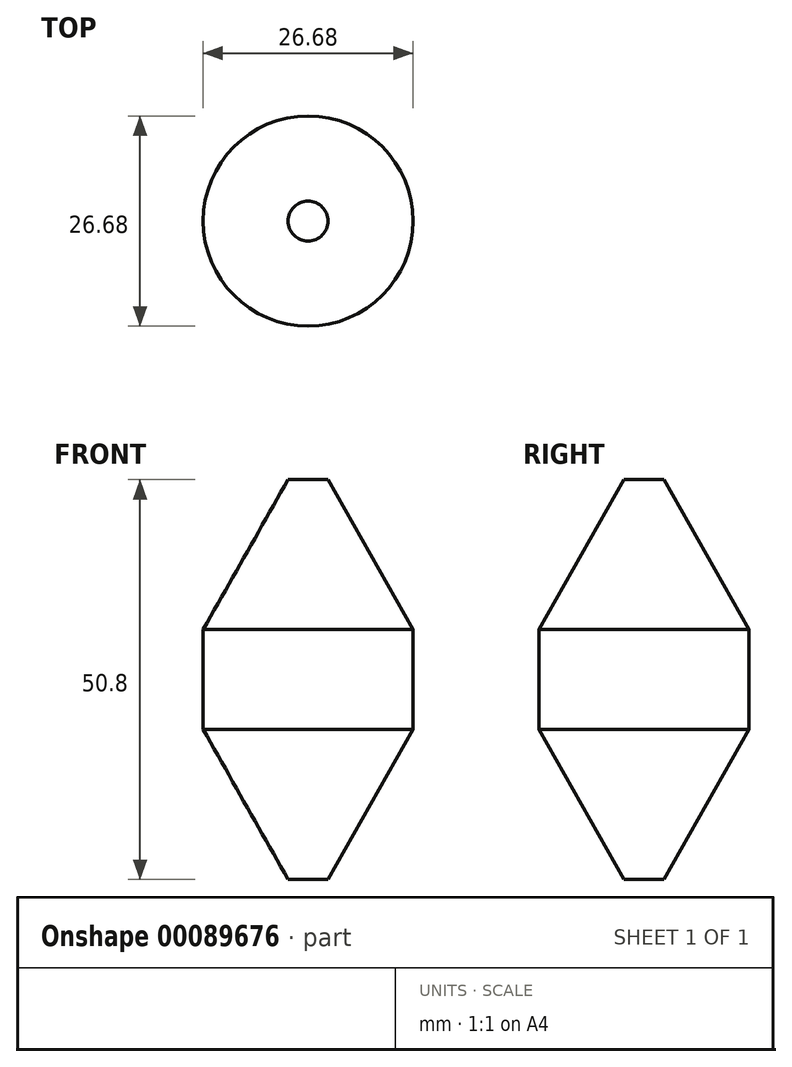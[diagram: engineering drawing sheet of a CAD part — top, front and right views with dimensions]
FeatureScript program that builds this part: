
annotation { "Feature Type Name" : "Feature", "Feature Type Description" : "" }
export const myFeature = defineFeature(function(context is Context, id is Id, definition is map)
    precondition{}
    {
        {
            var Q0;
            Q0=qCreatedBy(makeId("Top.planeOp"),FACE);
            var sketch = newSketch(context, id + "F0", { "sketchPlane" : qUnion([Q0])});
            skCircle(sketch, "E0", {"center": v(0, 0) * mm, "radius": 13.34 * mm});
            skSolve(sketch);
        }
        {
            var Q0;
            Q0 = qSketchRegion(id + "F0", true);
            extrude(context, id + "F1", {"entities" : qUnion([Q0]), "depth" : 6.35 * mm});
        }
        {
            var Q0;
            Q0=qCreatedBy(makeId("Right.planeOp"),FACE);
            cPlane(context, id + "F2", {"entities" : qUnion([Q0]), "cplaneType" : CPlaneType.OFFSET, "offset" : 8.9 * mm, "width" : 152.4 * mm, "height" : 152.4 * mm});
        }
        {
            var Q0;
            Q0=qCreatedBy(makeId("Right.planeOp"),FACE);
            var sketch = newSketch(context, id + "F4", { "sketchPlane" : qUnion([Q0])});
            skLineSegment(sketch, "E1", {"start": v(0, 6.35) * mm, "end": v(0, 25.4) * mm});
            skLineSegment(sketch, "E2", {"start": v(13.33, 6.35) * mm, "end": v(0, 6.35) * mm});
            skLineSegment(sketch, "E3", {"start": v(0, 25.4) * mm, "end": v(2.54, 25.4) * mm});
            skLineSegment(sketch, "E4", {"start": v(2.54, 25.4) * mm, "end": v(13.33, 6.35) * mm});
            skSolve(sketch);
        }
        {
            var Q0;
            Q0=qCreatedBy(makeId("Right.planeOp"),FACE);
            var sketch = newSketch(context, id + "F5", { "sketchPlane" : qUnion([Q0])});
            skLineSegment(sketch, "E5", {"start": v(0, 0) * mm, "end": v(0, 49.58) * mm});
            skSolve(sketch);
        }
        {
            var Q0;
            Q0 = qSketchRegion(id + "F4", true);
            var Q1;
            Q1=sQuery(id+"F5.wireOp",EDGE,"E5");
            revolve(context, id + "F6", {"operationType" : NewBodyOperationType.ADD, "entities" : qUnion([Q0]), "axis" : qUnion([Q1]), "revolveType" : RevolveType.FULL});
        }
        {
            var Q0;
            Q0=makeQuery(id+"F1.opExtrude","SWEPT_BODY",BODY,{"disambiguationData":[OSD([sQuery(id+"F0.wireOp",EDGE,"E0")])]});
            var Q1;
            Q1=qCreatedBy(makeId("Top.planeOp"),FACE);
            mirror(context, id + "F7", {"operationType" : NewBodyOperationType.ADD, "entities" : qUnion([Q0]), "mirrorPlane" : qUnion([Q1])});
        }
    });
